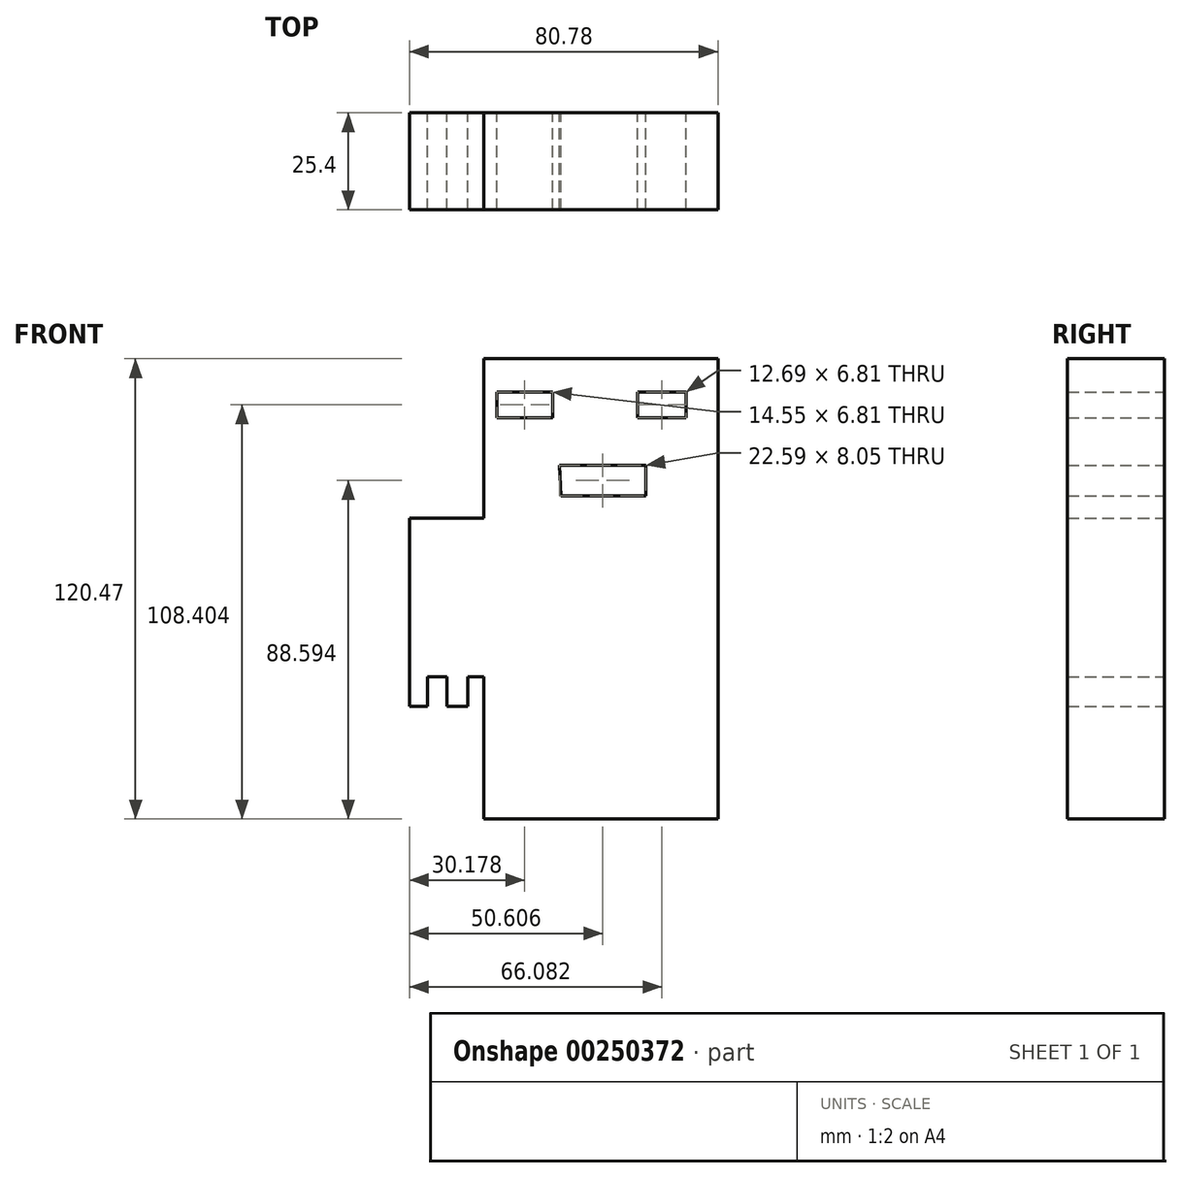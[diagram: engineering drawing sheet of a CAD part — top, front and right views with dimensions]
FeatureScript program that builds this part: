
annotation { "Feature Type Name" : "Feature", "Feature Type Description" : "" }
export const myFeature = defineFeature(function(context is Context, id is Id, definition is map)
    precondition{}
    {
        {
            var Q0;
            Q0=qCreatedBy(makeId("Front.planeOp"),FACE);
            var sketch = newSketch(context, id + "F0", { "sketchPlane" : qUnion([Q0])});
            skLineSegment(sketch, "E0", {"start": v(29.71, 45.03) * mm, "end": v(29.71, 3.25) * mm});
            skLineSegment(sketch, "E1", {"start": v(29.71, 3.25) * mm, "end": v(-31.57, 3.25) * mm});
            skLineSegment(sketch, "E2", {"start": v(-31.57, 3.25) * mm, "end": v(-31.57, 45.03) * mm});
            skPoint(sketch, "E3.end.orphan", {"position": v(-27.55, 45.03) * mm});
            skLineSegment(sketch, "E4", {"start": v(-31.57, 45.03) * mm, "end": v(29.71, 45.03) * mm});
            skLineSegment(sketch, "E5", {"start": v(-31.57, 3.25) * mm, "end": v(-31.57, -38.23) * mm});
            skLineSegment(sketch, "E6", {"start": v(-31.57, -38.23) * mm, "end": v(29.71, -38.23) * mm});
            skLineSegment(sketch, "E7", {"start": v(29.71, -38.23) * mm, "end": v(29.71, 3.25) * mm});
            skLineSegment(sketch, "E8", {"start": v(-13.62, 36.37) * mm, "end": v(-13.62, 29.56) * mm});
            skLineSegment(sketch, "E9", {"start": v(-13.62, 29.56) * mm, "end": v(-28.17, 29.56) * mm});
            skLineSegment(sketch, "E10", {"start": v(-28.17, 29.56) * mm, "end": v(-28.17, 36.37) * mm});
            skLineSegment(sketch, "E11", {"start": v(8.67, 29.56) * mm, "end": v(21.36, 29.56) * mm});
            skPoint(sketch, "E12.start.orphan", {"position": v(8.67, 36.37) * mm});
            skLineSegment(sketch, "E13", {"start": v(8.67, 29.56) * mm, "end": v(8.67, 36.37) * mm});
            skLineSegment(sketch, "E14", {"start": v(8.67, 36.37) * mm, "end": v(21.36, 36.37) * mm});
            skLineSegment(sketch, "E15", {"start": v(21.36, 36.37) * mm, "end": v(21.36, 29.56) * mm});
            skLineSegment(sketch, "E16", {"start": v(-11.76, 17.18) * mm, "end": v(10.83, 17.18) * mm});
            skLineSegment(sketch, "E17", {"start": v(10.83, 17.18) * mm, "end": v(10.83, 9.13) * mm});
            skLineSegment(sketch, "E18", {"start": v(10.83, 9.13) * mm, "end": v(-11.45, 9.13) * mm});
            skLineSegment(sketch, "E19", {"start": v(-11.45, 9.13) * mm, "end": v(-11.76, 17.18) * mm});
            skLineSegment(sketch, "E20", {"start": v(-7.12, 17.18) * mm, "end": v(-7.12, 9.13) * mm});
            skLineSegment(sketch, "E21", {"start": v(0, 17.18) * mm, "end": v(0, 9.13) * mm});
            skLineSegment(sketch, "E22", {"start": v(5.26, 17.18) * mm, "end": v(5.26, 9.13) * mm});
            skLineSegment(sketch, "E23", {"start": v(-3.71, 9.13) * mm, "end": v(-3.71, 17.18) * mm});
            skLineSegment(sketch, "E24", {"start": v(-31.57, -38.23) * mm, "end": v(-31.57, -65.46) * mm});
            skLineSegment(sketch, "E25", {"start": v(-31.57, -65.46) * mm, "end": v(0, -65.46) * mm});
            skLineSegment(sketch, "E26", {"start": v(0, -65.46) * mm, "end": v(0, -38.23) * mm});
            skLineSegment(sketch, "E27", {"start": v(29.71, -38.23) * mm, "end": v(29.71, -65.46) * mm});
            skLineSegment(sketch, "E28", {"start": v(29.71, -65.46) * mm, "end": v(2.17, -65.46) * mm});
            skLineSegment(sketch, "E29", {"start": v(2.17, -65.46) * mm, "end": v(0, -65.46) * mm});
            skLineSegment(sketch, "E30", {"start": v(29.71, 3.25) * mm, "end": v(48.28, 3.25) * mm});
            skLineSegment(sketch, "E31", {"start": v(48.28, 3.25) * mm, "end": v(48.28, -38.53) * mm});
            skLineSegment(sketch, "E32", {"start": v(-31.57, 3.25) * mm, "end": v(-51.07, 3.25) * mm});
            skLineSegment(sketch, "E33", {"start": v(-51.07, 3.25) * mm, "end": v(-51.07, -38.23) * mm});
            skLineSegment(sketch, "E34", {"start": v(-51.07, -38.23) * mm, "end": v(-31.57, -38.23) * mm});
            skLineSegment(sketch, "E35", {"start": v(-51.07, -38.23) * mm, "end": v(-51.07, -45.97) * mm});
            skLineSegment(sketch, "E36", {"start": v(-51.07, -45.97) * mm, "end": v(-46.37, -45.97) * mm});
            skLineSegment(sketch, "E37", {"start": v(-46.37, -45.97) * mm, "end": v(-46.37, -38.23) * mm});
            skLineSegment(sketch, "E38", {"start": v(-41.32, -38.23) * mm, "end": v(-41.32, -45.97) * mm});
            skLineSegment(sketch, "E39", {"start": v(-41.32, -45.97) * mm, "end": v(-35.8, -45.97) * mm});
            skLineSegment(sketch, "E40", {"start": v(-35.8, -45.97) * mm, "end": v(-35.8, -38.23) * mm});
            skLineSegment(sketch, "E41", {"start": v(48.28, -38.53) * mm, "end": v(48.28, -45.97) * mm});
            skLineSegment(sketch, "E42", {"start": v(39, -38.53) * mm, "end": v(39, -45.97) * mm});
            skPoint(sketch, "E42.startSnap0", {"position": v(39, -38.38) * mm});
            skLineSegment(sketch, "E43", {"start": v(39, -45.97) * mm, "end": v(34.02, -45.97) * mm});
            skLineSegment(sketch, "E44", {"start": v(34.02, -45.97) * mm, "end": v(34.02, -38.3) * mm});
            skPoint(sketch, "E45.end.orphan", {"position": v(42.05, -38.53) * mm});
            skLineSegment(sketch, "E46", {"start": v(48.28, -45.97) * mm, "end": v(43.63, -45.97) * mm});
            skLineSegment(sketch, "E47", {"start": v(43.63, -45.97) * mm, "end": v(43.63, -38.53) * mm});
            skLineSegment(sketch, "E48", {"start": v(-31.57, -65.46) * mm, "end": v(-31.57, -75.44) * mm});
            skLineSegment(sketch, "E49", {"start": v(-31.57, -75.44) * mm, "end": v(0, -75.44) * mm});
            skLineSegment(sketch, "E50", {"start": v(0, -75.44) * mm, "end": v(0, -65.46) * mm});
            skLineSegment(sketch, "E51", {"start": v(29.71, -65.46) * mm, "end": v(29.71, -75.44) * mm});
            skLineSegment(sketch, "E52", {"start": v(29.71, -75.44) * mm, "end": v(0, -75.44) * mm});
            skPoint(sketch, "E53.start.orphan", {"position": v(-27.24, 36.37) * mm});
            skLineSegment(sketch, "E54", {"start": v(-28.17, 36.37) * mm, "end": v(-13.62, 36.37) * mm});
            skLineSegment(sketch, "E55.trimOffspring", {"start": v(34.02, -38.3) * mm, "end": v(29.71, -38.23) * mm});
            skLineSegment(sketch, "E56", {"start": v(34.02, -38.3) * mm, "end": v(42.05, -38.53) * mm});
            skLineSegment(sketch, "E57", {"start": v(43.63, -38.53) * mm, "end": v(48.28, -38.53) * mm});
            skSolve(sketch);
        }
        {
            var Q0;
            Q0=makeQuery(id+"F0.imprint","IMPRINT",FACE,{"disambiguationData":[TD([[makeQuery(id+"F0.imprint","IMPRINT",EDGE,{"derivedFrom":sQuery(id+"F0.wireOp",EDGE,"E1")}),1.0]])]});
            var Q1;
            {var subQ3=sQuery(id+"F0.wireOp",EDGE,"E7");Q1=makeQuery(id+"F0.imprint","IMPRINT",FACE,{"disambiguationData":[TD([[makeQuery(id+"F0.imprint","IMPRINT",EDGE,{"derivedFrom":subQ3}),-1.0]])]});}
            var Q2;
            {var subQ3=sQuery(id+"F0.wireOp",EDGE,"E5");Q2=makeQuery(id+"F0.imprint","IMPRINT",FACE,{"disambiguationData":[TD([[makeQuery(id+"F0.imprint","IMPRINT",EDGE,{"derivedFrom":subQ3}),-1.0]])]});}
            var Q3;
            {var subQ2=sQuery(id+"F0.wireOp",EDGE,"E26");Q3=makeQuery(id+"F0.imprint","IMPRINT",FACE,{"disambiguationData":[TD([[makeQuery(id+"F0.imprint","IMPRINT",EDGE,{"derivedFrom":subQ2}),-1.0]])]});}
            var Q4;
            {var subQ0=sQuery(id+"F0.wireOp",EDGE,"E24");Q4=makeQuery(id+"F0.imprint","IMPRINT",FACE,{"disambiguationData":[TD([[makeQuery(id+"F0.imprint","IMPRINT",EDGE,{"derivedFrom":subQ0}),1.0]])]});}
            var Q5;
            Q5=makeQuery(id+"F0.imprint","IMPRINT",FACE,{"disambiguationData":[TD([[makeQuery(id+"F0.imprint","IMPRINT",EDGE,{"derivedFrom":sQuery(id+"F0.wireOp",EDGE,"E28")}),1.0]])]});
            var Q6;
            Q6=makeQuery(id+"F0.imprint","IMPRINT",FACE,{"disambiguationData":[TD([[makeQuery(id+"F0.imprint","IMPRINT",EDGE,{"derivedFrom":sQuery(id+"F0.wireOp",EDGE,"E25")}),-1.0]])]});
            var Q7;
            Q7=makeQuery(id+"F0.imprint","IMPRINT",FACE,{"disambiguationData":[TD([[makeQuery(id+"F0.imprint","IMPRINT",EDGE,{"derivedFrom":sQuery(id+"F0.wireOp",EDGE,"E0")}),-1.0]])]});
            var Q8;
            {var subQ0=sQuery(id+"F0.wireOp",EDGE,"E35");Q8=makeQuery(id+"F0.imprint","IMPRINT",FACE,{"disambiguationData":[TD([[makeQuery(id+"F0.imprint","IMPRINT",EDGE,{"derivedFrom":subQ0}),1.0]])]});}
            var Q9;
            {var subQ0=sQuery(id+"F0.wireOp",EDGE,"E38");Q9=makeQuery(id+"F0.imprint","IMPRINT",FACE,{"disambiguationData":[TD([[makeQuery(id+"F0.imprint","IMPRINT",EDGE,{"derivedFrom":subQ0}),1.0]])]});}
            extrude(context, id + "F1", {"entities" : qUnion([Q0, Q1, Q2, Q3, Q4, Q5, Q6, Q7, Q8, Q9]), "depth" : 25.4 * mm});
        }
    });
